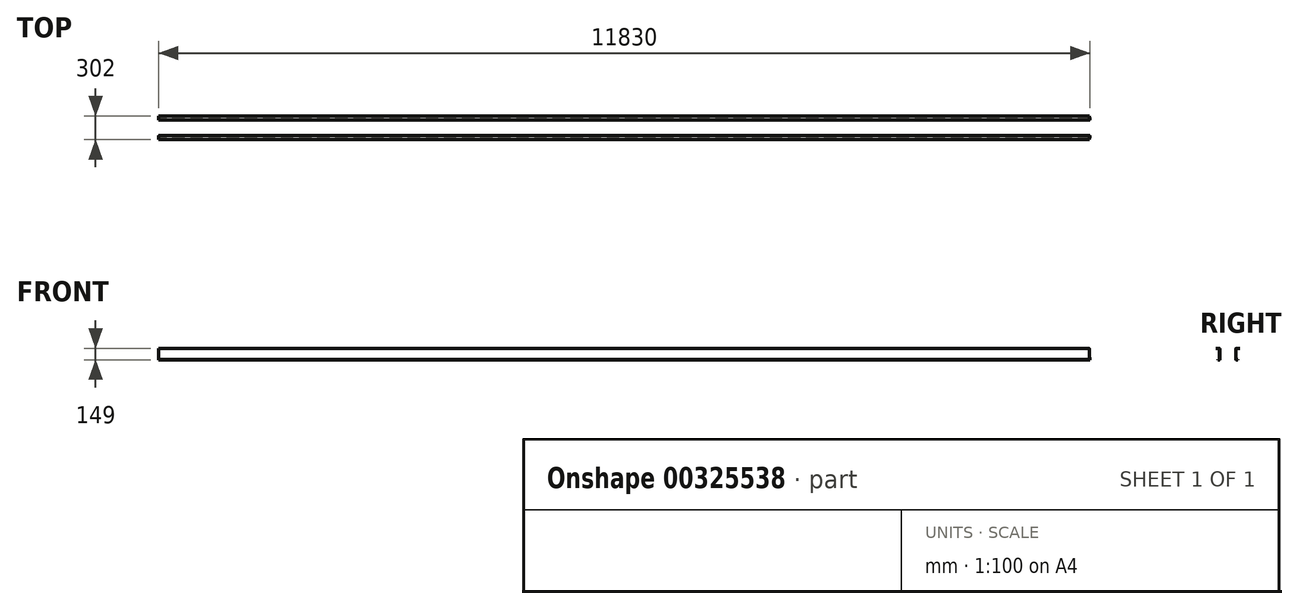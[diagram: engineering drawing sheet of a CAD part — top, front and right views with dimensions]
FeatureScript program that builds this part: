
annotation { "Feature Type Name" : "Feature", "Feature Type Description" : "" }
export const myFeature = defineFeature(function(context is Context, id is Id, definition is map)
    precondition{}
    {
        {
            var Q0;
            Q0=qCreatedBy(makeId("Right.planeOp"),FACE);
            var sketch = newSketch(context, id + "F0", { "sketchPlane" : qUnion([Q0])});
            skLineSegment(sketch, "E0", {"start": v(-32.86, 14.64) * mm, "end": v(13.14, 14.64) * mm});
            skLineSegment(sketch, "E1", {"start": v(18.14, 9.64) * mm, "end": v(18.14, -129.36) * mm});
            skLineSegment(sketch, "E2", {"start": v(13.14, -134.36) * mm, "end": v(-10.86, -134.36) * mm});
            skLineSegment(sketch, "E3", {"start": v(-32.86, 14.64) * mm, "end": v(-32.86, 9.64) * mm});
            skLineSegment(sketch, "E4.0", {"start": v(8.14, -129.36) * mm, "end": v(-10.86, -129.36) * mm});
            skLineSegment(sketch, "E4.1", {"start": v(13.14, 4.64) * mm, "end": v(13.14, -124.36) * mm});
            skLineSegment(sketch, "E4.2", {"start": v(-32.86, 9.64) * mm, "end": v(8.14, 9.64) * mm});
            skLineSegment(sketch, "E5", {"start": v(-10.86, -129.36) * mm, "end": v(-10.86, -134.36) * mm});
            skPoint(sketch, "E6.visualSharp", {"position": v(13.14, 9.64) * mm});
            skArc(sketch, "E6.filletArc", {"start": v(13.14, 4.64) * mm, "mid": v(11.68, 8.17) * mm, "end": v(8.14, 9.64) * mm});
            skPoint(sketch, "E7.visualSharp", {"position": v(18.14, 14.64) * mm});
            skArc(sketch, "E7.filletArc", {"start": v(18.14, 9.64) * mm, "mid": v(16.68, 13.17) * mm, "end": v(13.14, 14.64) * mm});
            skPoint(sketch, "E8.visualSharp", {"position": v(13.14, -129.36) * mm});
            skArc(sketch, "E8.filletArc", {"start": v(8.14, -129.36) * mm, "mid": v(11.68, -127.9) * mm, "end": v(13.14, -124.36) * mm});
            skPoint(sketch, "E9.visualSharp", {"position": v(18.14, -134.36) * mm});
            skArc(sketch, "E9.filletArc", {"start": v(13.14, -134.36) * mm, "mid": v(16.68, -132.9) * mm, "end": v(18.14, -129.36) * mm});
            skSolve(sketch);
        }
        {
            var Q0;
            Q0 = qSketchRegion(id + "F0", true);
            extrude(context, id + "F1", {"entities" : qUnion([Q0]), "depth" : 11830 * mm});
        }
        {
            var Q0;
            Q0=makeQuery(id+"F1.opExtrude","SWEPT_FACE",FACE,{"disambiguationData":[OSD([sQuery(id+"F0.wireOp",EDGE,"E1")])]});
            var sketch = newSketch(context, id + "F2", { "sketchPlane" : qUnion([Q0])});
            skLineSegment(sketch, "E10", {"start": v(-11830, 9.64) * mm, "end": v(-11830, -103.36) * mm});
            skLineSegment(sketch, "E11", {"start": v(-11830, -103.36) * mm, "end": v(-11830, -103.36) * mm});
            skLineSegment(sketch, "E12", {"start": v(-11825, 20.85) * mm, "end": v(-11830, 20.85) * mm});
            skLineSegment(sketch, "E13", {"start": v(-11830, 20.85) * mm, "end": v(-11830, 9.64) * mm});
            skPoint(sketch, "E14.visualSharp", {"position": v(-11825, -103.36) * mm});
            skLineSegment(sketch, "E15", {"start": v(-11830, 20.85) * mm, "end": v(-11830, -103.36) * mm});
            skLineSegment(sketch, "E16", {"start": v(-11830, -103.36) * mm, "end": v(-11829, -103.36) * mm});
            skLineSegment(sketch, "E17", {"start": v(-11824, -98.36) * mm, "end": v(-11824, 20.85) * mm});
            skLineSegment(sketch, "E18", {"start": v(-11824, 20.85) * mm, "end": v(-11825, 20.85) * mm});
            skPoint(sketch, "E19.visualSharp", {"position": v(-11824, -103.36) * mm});
            skArc(sketch, "E19.filletArc", {"start": v(-11829, -103.36) * mm, "mid": v(-11825.46, -101.9) * mm, "end": v(-11824, -98.36) * mm});
            skSolve(sketch);
        }
        {
            var Q0;
            {var subQ4=sQuery(id+"F2.wireOp",EDGE,"E10");Q0=makeQuery(id+"F2.imprint","IMPRINT",FACE,{"disambiguationData":[TD([[makeQuery(id+"F2.imprint","IMPRINT",EDGE,{"derivedFrom":subQ4}),1.0]])]});}
            var Q1;
            Q1=makeQuery(id+"F2.imprint","IMPRINT",FACE,{"disambiguationData":[TD([[makeQuery(id+"F2.imprint","IMPRINT",EDGE,{"derivedFrom":sQuery(id+"F2.wireOp",EDGE,"E12")}),1.0]])]});
            extrude(context, id + "F3", {"entities" : qUnion([Q0, Q1]), "operationType" : NewBodyOperationType.REMOVE, "oppositeDirection" : true, "depth" : 51 * mm});
        }
        {
            var Q0;
            Q0=makeQuery(id+"F1.opExtrude","SWEPT_FACE",FACE,{"disambiguationData":[OSD([sQuery(id+"F0.wireOp",EDGE,"E1")])]});
            cPlane(context, id + "F4", {"entities" : qUnion([Q0]), "cplaneType" : CPlaneType.OFFSET, "offset" : 100 * mm, "width" : 150 * mm, "height" : 150 * mm});
        }
        {
            var Q0;
            Q0=makeQuery(id+"F1.opExtrude","SWEPT_BODY",BODY,{"disambiguationData":[OSD([sQuery(id+"F0.wireOp",EDGE,"E0"),sQuery(id+"F0.wireOp",EDGE,"E1"),sQuery(id+"F0.wireOp",EDGE,"E2"),sQuery(id+"F0.wireOp",EDGE,"E3"),sQuery(id+"F0.wireOp",EDGE,"E4.0"),sQuery(id+"F0.wireOp",EDGE,"E4.1"),sQuery(id+"F0.wireOp",EDGE,"E4.2"),sQuery(id+"F0.wireOp",EDGE,"E5"),sQuery(id+"F0.wireOp",EDGE,"E6.filletArc"),sQuery(id+"F0.wireOp",EDGE,"E7.filletArc"),sQuery(id+"F0.wireOp",EDGE,"E8.filletArc"),sQuery(id+"F0.wireOp",EDGE,"E9.filletArc")])]});
            var Q1;
            Q1=qCreatedBy(id+"F4.planeOp",FACE);
            mirror(context, id + "F5", {"entities" : qUnion([Q0]), "mirrorPlane" : qUnion([Q1])});
        }
    });
